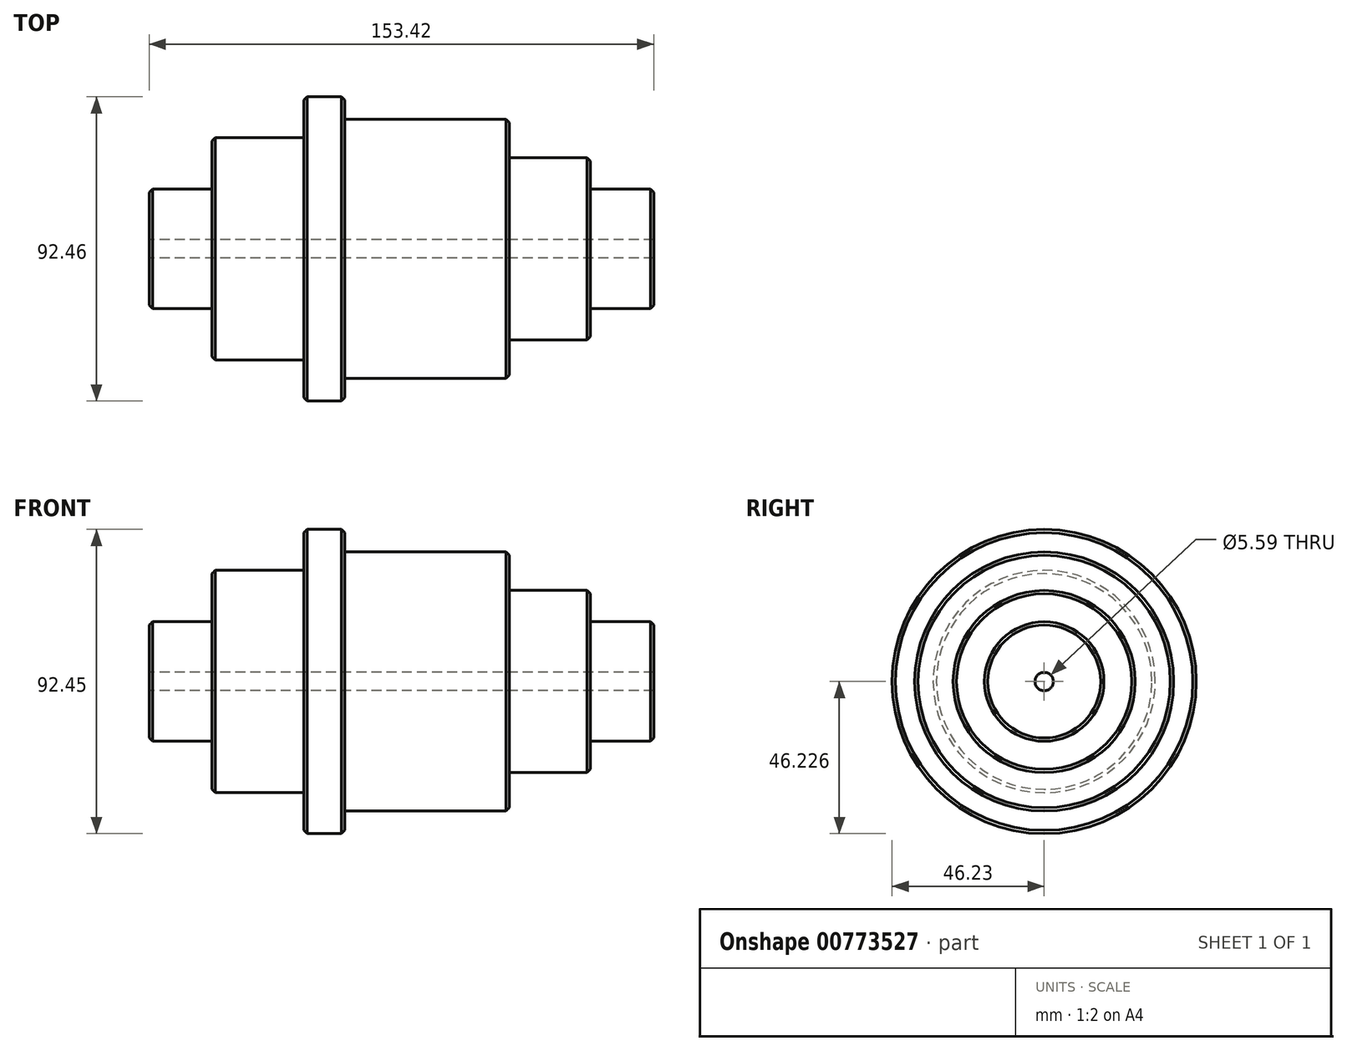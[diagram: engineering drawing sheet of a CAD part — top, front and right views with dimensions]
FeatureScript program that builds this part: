
annotation { "Feature Type Name" : "Feature", "Feature Type Description" : "" }
export const myFeature = defineFeature(function(context is Context, id is Id, definition is map)
    precondition{}
    {
        {
            var Q0;
            Q0=qCreatedBy(makeId("Front.planeOp"),FACE);
            var sketch = newSketch(context, id + "F0", { "sketchPlane" : qUnion([Q0])});
            skLineSegment(sketch, "E0", {"start": v(-80.14, -15.37) * mm, "end": v(73.28, -15.37) * mm});
            skLineSegment(sketch, "E1", {"start": v(-80.14, -15.37) * mm, "end": v(-80.14, 0) * mm});
            skLineSegment(sketch, "E2", {"start": v(-80.14, 0) * mm, "end": v(-61.09, 0) * mm});
            skLineSegment(sketch, "E3", {"start": v(-61.09, 0) * mm, "end": v(-61.09, 15.62) * mm});
            skLineSegment(sketch, "E4", {"start": v(-61.09, 15.62) * mm, "end": v(-33.15, 15.62) * mm});
            skLineSegment(sketch, "E5", {"start": v(-33.15, 15.62) * mm, "end": v(-33.15, 28.06) * mm});
            skLineSegment(sketch, "E6", {"start": v(-33.15, 28.06) * mm, "end": v(-20.7, 28.06) * mm});
            skLineSegment(sketch, "E7", {"start": v(-20.7, 28.06) * mm, "end": v(-20.7, 21.2) * mm});
            skLineSegment(sketch, "E8", {"start": v(-20.7, 21.2) * mm, "end": v(29.34, 21.2) * mm});
            skLineSegment(sketch, "E9", {"start": v(29.34, 21.2) * mm, "end": v(29.34, 9.52) * mm});
            skLineSegment(sketch, "E10", {"start": v(29.34, 9.52) * mm, "end": v(53.98, 9.52) * mm});
            skLineSegment(sketch, "E11", {"start": v(53.98, 9.52) * mm, "end": v(53.98, 0) * mm});
            skLineSegment(sketch, "E12", {"start": v(53.98, 0) * mm, "end": v(73.28, 0) * mm});
            skLineSegment(sketch, "E13", {"start": v(73.28, 0) * mm, "end": v(73.28, -15.37) * mm});
            skLineSegment(sketch, "E14", {"start": v(-83.19, -18.16) * mm, "end": v(76.58, -18.16) * mm, "construction": true});
            skSolve(sketch);
        }
        {
            var Q0;
            Q0=makeQuery(id+"F0.imprint","IMPRINT",FACE,{"disambiguationData":[TD([[makeQuery(id+"F0.imprint","IMPRINT",EDGE,{"derivedFrom":sQuery(id+"F0.wireOp",EDGE,"E0")}),1.0]])]});
            var Q1;
            Q1=sQuery(id+"F0.wireOp",EDGE,"E14");
            revolve(context, id + "F1", {"surfaceOperationType" : NewSurfaceOperationType.NEW, "entities" : qUnion([Q0]), "axis" : qUnion([Q1]), "revolveType" : RevolveType.FULL});
        }
        {
            var Q0;
            Q0=makeQuery(id+"F1.opRevolve","SWEPT_EDGE",EDGE,{"disambiguationData":[OSD([sQuery(id+"F0.wireOp",EDGE,"E1"),sQuery(id+"F0.wireOp",EDGE,"E2")])]});
            chamfer(context, id + "F2", {"entities" : qUnion([Q0]), "width" : 1.02 * mm, "tangentPropagation" : true});
        }
        {
            var Q0;
            Q0=makeQuery(id+"F1.opRevolve","SWEPT_EDGE",EDGE,{"disambiguationData":[OSD([sQuery(id+"F0.wireOp",EDGE,"E3"),sQuery(id+"F0.wireOp",EDGE,"E4")])]});
            chamfer(context, id + "F3", {"entities" : qUnion([Q0]), "width" : 1.02 * mm, "tangentPropagation" : true});
        }
        {
            var Q0;
            Q0=makeQuery(id+"F1.opRevolve","SWEPT_EDGE",EDGE,{"disambiguationData":[OSD([sQuery(id+"F0.wireOp",EDGE,"E5"),sQuery(id+"F0.wireOp",EDGE,"E6")])]});
            chamfer(context, id + "F4", {"entities" : qUnion([Q0]), "width" : 1.02 * mm, "tangentPropagation" : true});
        }
        {
            var Q0;
            Q0=makeQuery(id+"F1.opRevolve","SWEPT_EDGE",EDGE,{"disambiguationData":[OSD([sQuery(id+"F0.wireOp",EDGE,"E6"),sQuery(id+"F0.wireOp",EDGE,"E7")])]});
            chamfer(context, id + "F5", {"entities" : qUnion([Q0]), "width" : 1.02 * mm, "tangentPropagation" : true});
        }
        {
            var Q0;
            Q0=makeQuery(id+"F1.opRevolve","SWEPT_EDGE",EDGE,{"disambiguationData":[OSD([sQuery(id+"F0.wireOp",EDGE,"E8"),sQuery(id+"F0.wireOp",EDGE,"E9")])]});
            chamfer(context, id + "F6", {"entities" : qUnion([Q0]), "width" : 1.02 * mm, "tangentPropagation" : true});
        }
        {
            var Q0;
            Q0=makeQuery(id+"F1.opRevolve","SWEPT_EDGE",EDGE,{"disambiguationData":[OSD([sQuery(id+"F0.wireOp",EDGE,"E10"),sQuery(id+"F0.wireOp",EDGE,"E11")])]});
            chamfer(context, id + "F7", {"entities" : qUnion([Q0]), "width" : 1.02 * mm, "tangentPropagation" : true});
        }
        {
            var Q0;
            Q0=makeQuery(id+"F1.opRevolve","SWEPT_EDGE",EDGE,{"disambiguationData":[OSD([sQuery(id+"F0.wireOp",EDGE,"E12"),sQuery(id+"F0.wireOp",EDGE,"E13")])]});
            chamfer(context, id + "F8", {"entities" : qUnion([Q0]), "width" : 1.02 * mm, "tangentPropagation" : true});
        }
    });
